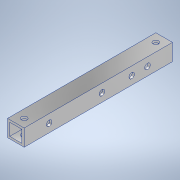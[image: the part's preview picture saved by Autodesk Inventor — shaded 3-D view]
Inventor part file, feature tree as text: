
AUTODESK INVENTOR PART (.ipt)
format: ipt  version: 2020.3 (Build 243373000, 373)  size: 139,776 bytes
history: native  units: mm
features: sketch x4, hole x3, other x1, extrude x1
ambient origin geometry x8: Origin, YZ Plane, XZ Plane, XY Plane, X Axis, Y Axis, Z Axis, Center Point
bodies: Body1 (feature_tree)
feature tree (9):
  other  "ソリッド1"
  extrude  "押し出し1"  Depth=9.0mm
  hole  "穴1"  [1 undecoded]
  hole  "穴2"  [1 undecoded]
  hole  "穴3"  [1 undecoded]
  sketch  "スケッチ1"
  sketch  "スケッチ2"
  sketch  "スケッチ3"
  sketch  "スケッチ4"
note: 3 required parameter values undecoded (feature->parameter linkage not recoverable at this tier; creation-order binding heuristic only, values carry confidence <= 0.55)
